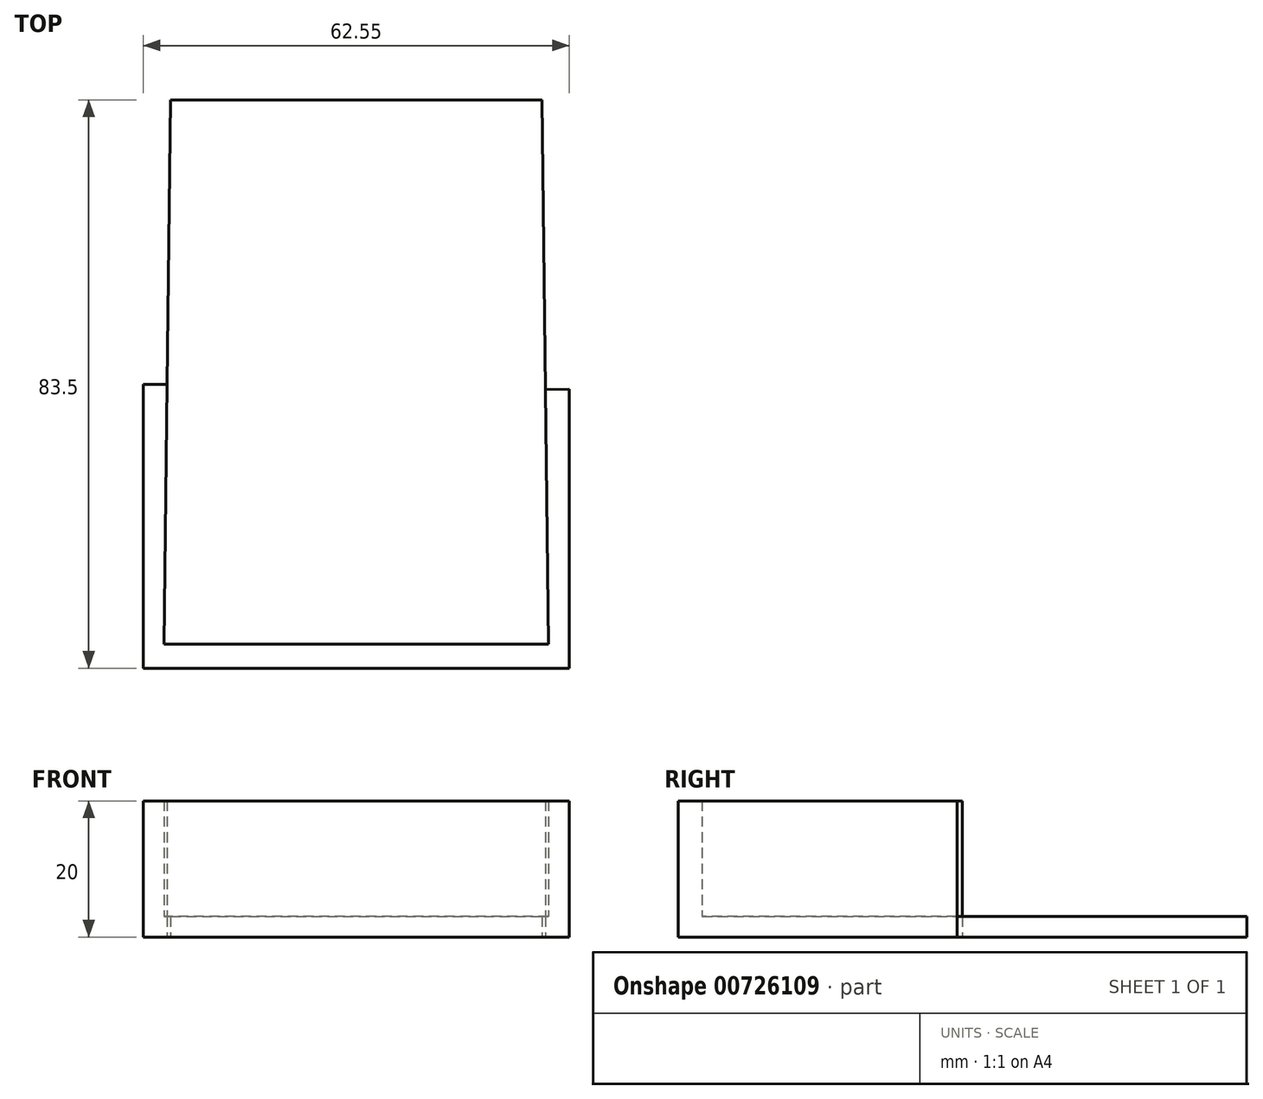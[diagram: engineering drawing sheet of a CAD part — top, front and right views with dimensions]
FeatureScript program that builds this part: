
annotation { "Feature Type Name" : "Feature", "Feature Type Description" : "" }
export const myFeature = defineFeature(function(context is Context, id is Id, definition is map)
    precondition{}
    {
        {
            var Q0;
            Q0=qCreatedBy(makeId("Top.planeOp"),FACE);
            var sketch = newSketch(context, id + "F0", { "sketchPlane" : qUnion([Q0])});
            skLineSegment(sketch, "E0", {"start": v(-27, 79.8) * mm, "end": v(27.5, 79.8) * mm});
            skLineSegment(sketch, "E1", {"start": v(27.5, 79.8) * mm, "end": v(28.5, -0.2) * mm});
            skLineSegment(sketch, "E2", {"start": v(28.5, -0.2) * mm, "end": v(-28, -0.2) * mm});
            skLineSegment(sketch, "E3", {"start": v(-28, -0.2) * mm, "end": v(-27, 79.8) * mm});
            skPoint(sketch, "E4", {"position": v(0.25, -0.2) * mm});
            skPoint(sketch, "E5", {"position": v(0.25, 79.8) * mm});
            skLineSegment(sketch, "E6", {"start": v(31.53, -3.7) * mm, "end": v(-31.02, -3.7) * mm});
            skLineSegment(sketch, "E7", {"start": v(-31.02, -3.7) * mm, "end": v(-31.02, 37.99) * mm});
            skLineSegment(sketch, "E8", {"start": v(31.53, -3.7) * mm, "end": v(31.53, 37.27) * mm});
            skLineSegment(sketch, "E9", {"start": v(-31.02, 14.7) * mm, "end": v(-31.02, 14.7) * mm});
            skLineSegment(sketch, "E10", {"start": v(-31.02, 37.99) * mm, "end": v(-27.52, 37.99) * mm});
            skLineSegment(sketch, "E11", {"start": v(31.53, 37.27) * mm, "end": v(28.03, 37.23) * mm});
            skSolve(sketch);
        }
        {
            var Q0;
            {var subQ1=sQuery(id+"F0.wireOp",EDGE,"E2");Q0=makeQuery(id+"F0.imprint","IMPRINT",FACE,{"disambiguationData":[TD([[makeQuery(id+"F0.imprint","IMPRINT",EDGE,{"derivedFrom":subQ1}),1.0]])]});}
            extrude(context, id + "F1", {"entities" : qUnion([Q0]), "depth" : 20 * mm, "offsetDistance" : 25 * mm});
        }
        {
            var Q0;
            {var subQ3=sQuery(id+"F0.wireOp",EDGE,"E0");Q0=makeQuery(id+"F0.imprint","IMPRINT",FACE,{"disambiguationData":[TD([[makeQuery(id+"F0.imprint","IMPRINT",EDGE,{"derivedFrom":subQ3}),-1.0]])]});}
            extrude(context, id + "F2", {"entities" : qUnion([Q0]), "operationType" : NewBodyOperationType.ADD, "depth" : 3 * mm, "offsetDistance" : 25 * mm});
        }
    });
